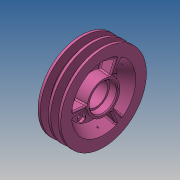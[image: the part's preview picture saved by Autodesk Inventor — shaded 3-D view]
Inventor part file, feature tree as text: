
AUTODESK INVENTOR PART (.ipt)
format: ipt  version: 2017 (Build 210142000, 142)  size: 677,888 bytes
history: native  units: mm
features: revolve x5, sketch x4, extrude x3, other x2, chamfer x2, plane x2, fillet x1, pattern_circular x1, projected_geometry x1
ambient origin geometry x8: Origin, YZ Plane, XZ Plane, XY Plane, X Axis, Y Axis, Z Axis, Center Point
bodies: Body1 (feature_tree), Body2 (feature_tree)
feature tree (21):
  other  "Sólido1"
  sketch  "Boceto1"  dims[d0=8.0mm d1=28.5mm]
  revolve  "Revolución1"  [1 undecoded]
  sketch  "Boceto2"  dims[d2=24.5mm d3=6.0mm]
  extrude  "Extrusión1"  Depth=6.0mm
  chamfer  "Chaflán1"  Distance=20.0mm
  extrude  "Extrusión2"  TaperAngle=90.0deg  [1 undecoded]
  extrude  "Extrusión3"  Depth=8.0mm
  chamfer  "Chaflán2"  Distance=3.0mm
  plane  "Plano de trabajo1"
  revolve  "Revolución3"  [1 undecoded]
  fillet  "Empalme1"  Radius=10.0mm
  plane  "Plano de trabajo2"
  revolve  "Revolución4"  [1 undecoded]
  revolve  "Revolución5"  [1 undecoded]
  pattern_circular  "Patrón circular1"  [2 undecoded]
  revolve  "Revolución2"  [1 undecoded]
  other  "espaciador"
  sketch  "Boceto3"  dims[d4=4.0mm]
  sketch  "Boceto4"  dims[d5=90.0mm d6=20.0mm d7=2.5mm d8=90.0deg d10=9.0mm d11=3.0mm d13=47.0mm d14=10.0mm d15=0.0mm d16=10.0mm d17=0.0mm d18=8.0mm d20=2.094395mm d24=44.5mm d25=44.0mm d26=8.0mm d27=12.0mm d28=16.0mm d29=8.0mm d30=90.0deg d31=24.0mm d32=30.0mm d33=17.790202mm d34=8.281806mm d35=3.0mm d36=0.0mm d37=60.0deg d38=2.094395mm d39=1.5mm d40=30.0mm d41=360.0deg d43=60.0deg d44=1.5mm d45=2.094395mm d46=1.0mm d47=2.0mm d48=45.0deg d49=0.4mm d50=2.0mm d51=45.0deg d52=4.0mm d53=70.0mm d54=3.0mm d55=90.0deg d56=120.0deg]
  projected_geometry  "Contorno proyectado1"
note: 8 required parameter values undecoded (feature->parameter linkage not recoverable at this tier; creation-order binding heuristic only, values carry confidence <= 0.55)